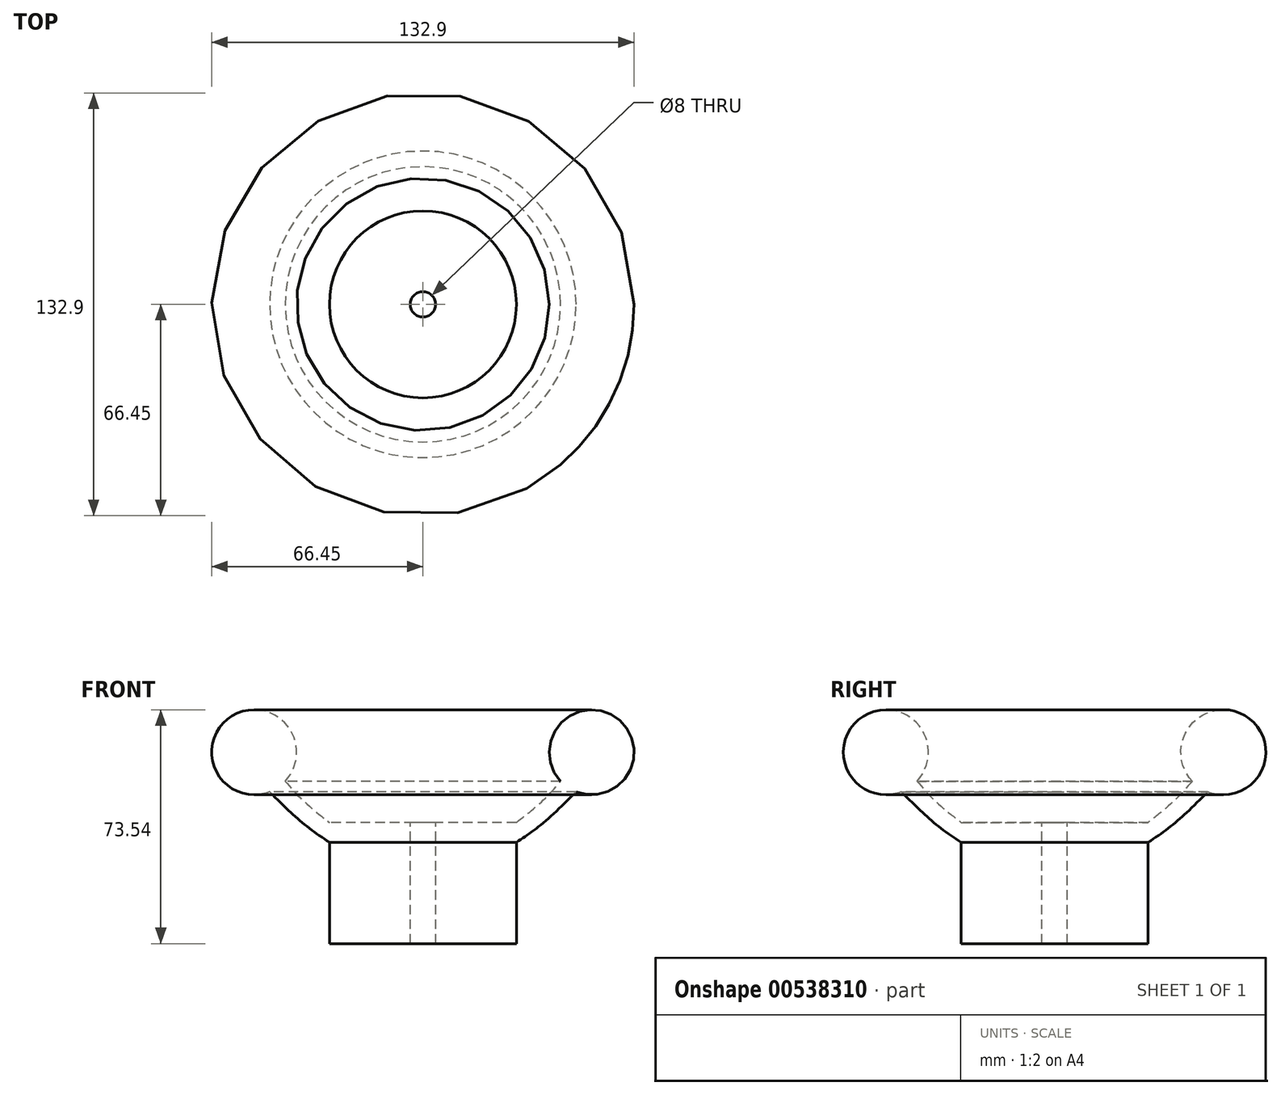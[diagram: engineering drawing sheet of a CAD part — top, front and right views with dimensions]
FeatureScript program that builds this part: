
annotation { "Feature Type Name" : "Feature", "Feature Type Description" : "" }
export const myFeature = defineFeature(function(context is Context, id is Id, definition is map)
    precondition{}
    {
        {
            var Q0;
            Q0=qCreatedBy(makeId("Front.planeOp"),FACE);
            var sketch = newSketch(context, id + "F0", { "sketchPlane" : qUnion([Q0])});
            skLineSegment(sketch, "E0.bottom", {"start": v(4, 0) * mm, "end": v(29.4, 0) * mm});
            skLineSegment(sketch, "E0.top", {"start": v(4, 38.1) * mm, "end": v(29.4, 38.1) * mm});
            skLineSegment(sketch, "E0.left", {"start": v(4, 0) * mm, "end": v(4, 38.1) * mm});
            skLineSegment(sketch, "E0.right", {"start": v(29.4, 0) * mm, "end": v(29.4, 31.86) * mm});
            skLineSegment(sketch, "E1", {"start": v(0, 109.62) * mm, "end": v(0, -110.32) * mm, "construction": true});
            skFitSpline(sketch, "E2", {"points": [v(29.4, 38.1) * mm, v(38.04, 45.29) * mm, v(44.67, 52.73) * mm], "startDerivative": vector(17.57, 13.6) * mm, "endDerivative": vector(12.93, 15.68) * mm});
            skFitSpline(sketch, "E3", {"points": [v(29.4, 31.86) * mm, v(38.04, 38.1) * mm, v(53.08, 52.73) * mm], "startDerivative": vector(19.71, 12.92) * mm, "endDerivative": vector(27.24, 27.99) * mm});
            skPoint(sketch, "E4.center.orphan", {"position": v(53.08, 60.17) * mm});
            skArc(sketch, "E5", {"start": v(48.2, 47.73) * mm, "mid": v(60.61, 71.22) * mm, "end": v(43.3, 51.07) * mm});
            skSolve(sketch);
        }
        {
            var Q0;
            Q0=makeQuery(id+"F0.imprint","IMPRINT",FACE,{"disambiguationData":[TD([[makeQuery(id+"F0.imprint","IMPRINT",EDGE,{"derivedFrom":sQuery(id+"F0.wireOp",EDGE,"E0.bottom")}),1.0]])]});
            var Q1;
            Q1=sQuery(id+"F0.wireOp",EDGE,"E1");
            revolve(context, id + "F1", {"entities" : qUnion([Q0]), "axis" : qUnion([Q1]), "revolveType" : RevolveType.FULL});
        }
    });
